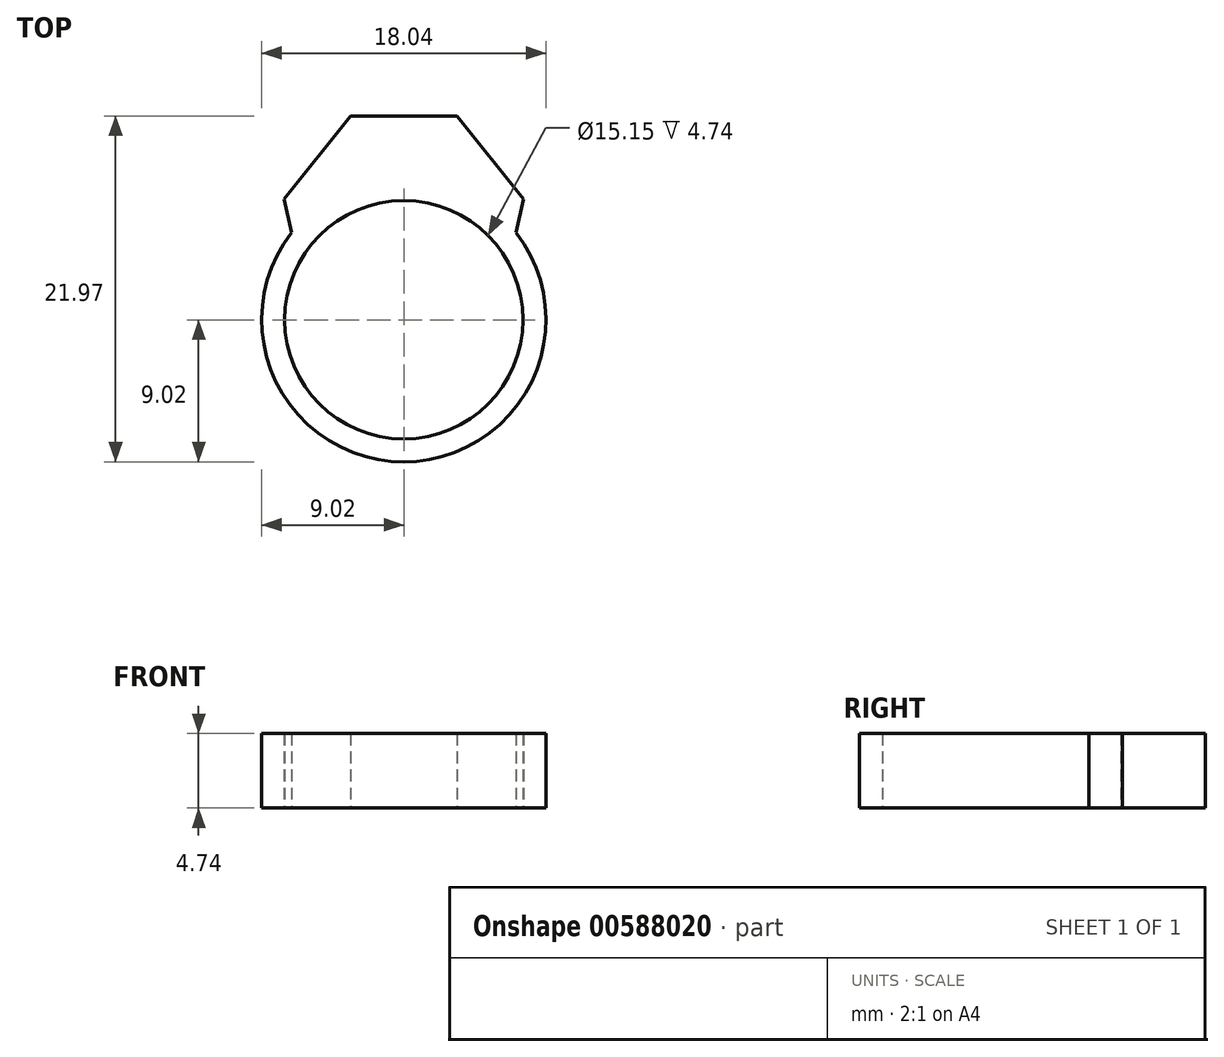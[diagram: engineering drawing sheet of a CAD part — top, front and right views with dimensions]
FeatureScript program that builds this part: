
annotation { "Feature Type Name" : "Feature", "Feature Type Description" : "" }
export const myFeature = defineFeature(function(context is Context, id is Id, definition is map)
    precondition{}
    {
        {
            var Q0;
            Q0=qCreatedBy(makeId("Top.planeOp"),FACE);
            var sketch = newSketch(context, id + "F0", { "sketchPlane" : qUnion([Q0])});
            skCircle(sketch, "E0", {"center": v(0, 0) * mm, "radius": 7.58 * mm});
            skCircle(sketch, "E1", {"center": v(0, 0) * mm, "radius": 9.02 * mm});
            skLineSegment(sketch, "E2.0", {"start": v(-3.39, 12.95) * mm, "end": v(3.39, 12.95) * mm});
            skLineSegment(sketch, "E2.1", {"start": v(3.39, 12.95) * mm, "end": v(7.61, 7.65) * mm});
            skLineSegment(sketch, "E2.2", {"start": v(7.61, 7.65) * mm, "end": v(7.13, 5.53) * mm});
            skLineSegment(sketch, "E2.6", {"start": v(-7.61, 7.65) * mm, "end": v(-3.39, 12.95) * mm});
            skPoint(sketch, "E2.0.midPoint", {"position": v(0, 12.95) * mm});
            skPoint(sketch, "E3.orphan", {"position": v(-6.1, 1.05) * mm});
            skLineSegment(sketch, "E4.trimOffspring", {"start": v(-7.13, 5.53) * mm, "end": v(-7.61, 7.65) * mm});
            skPoint(sketch, "E5.end.orphan", {"position": v(0, 5.92) * mm});
            skSolve(sketch);
        }
        {
            var Q0;
            Q0=makeQuery(id+"F0.imprint","IMPRINT",FACE,{"disambiguationData":[TD([[makeQuery(id+"F0.imprint","IMPRINT",EDGE,{"derivedFrom":sQuery(id+"F0.wireOp",EDGE,"E0")}),-1.0]])]});
            var Q1;
            Q1=makeQuery(id+"F0.imprint","IMPRINT",FACE,{"disambiguationData":[TD([[makeQuery(id+"F0.imprint","IMPRINT",EDGE,{"derivedFrom":sQuery(id+"F0.wireOp",EDGE,"E2.0")}),-1.0]])]});
            extrude(context, id + "F1", {"entities" : qUnion([Q0, Q1]), "depth" : 4.74 * mm, "offsetDistance" : 25 * mm});
        }
    });
